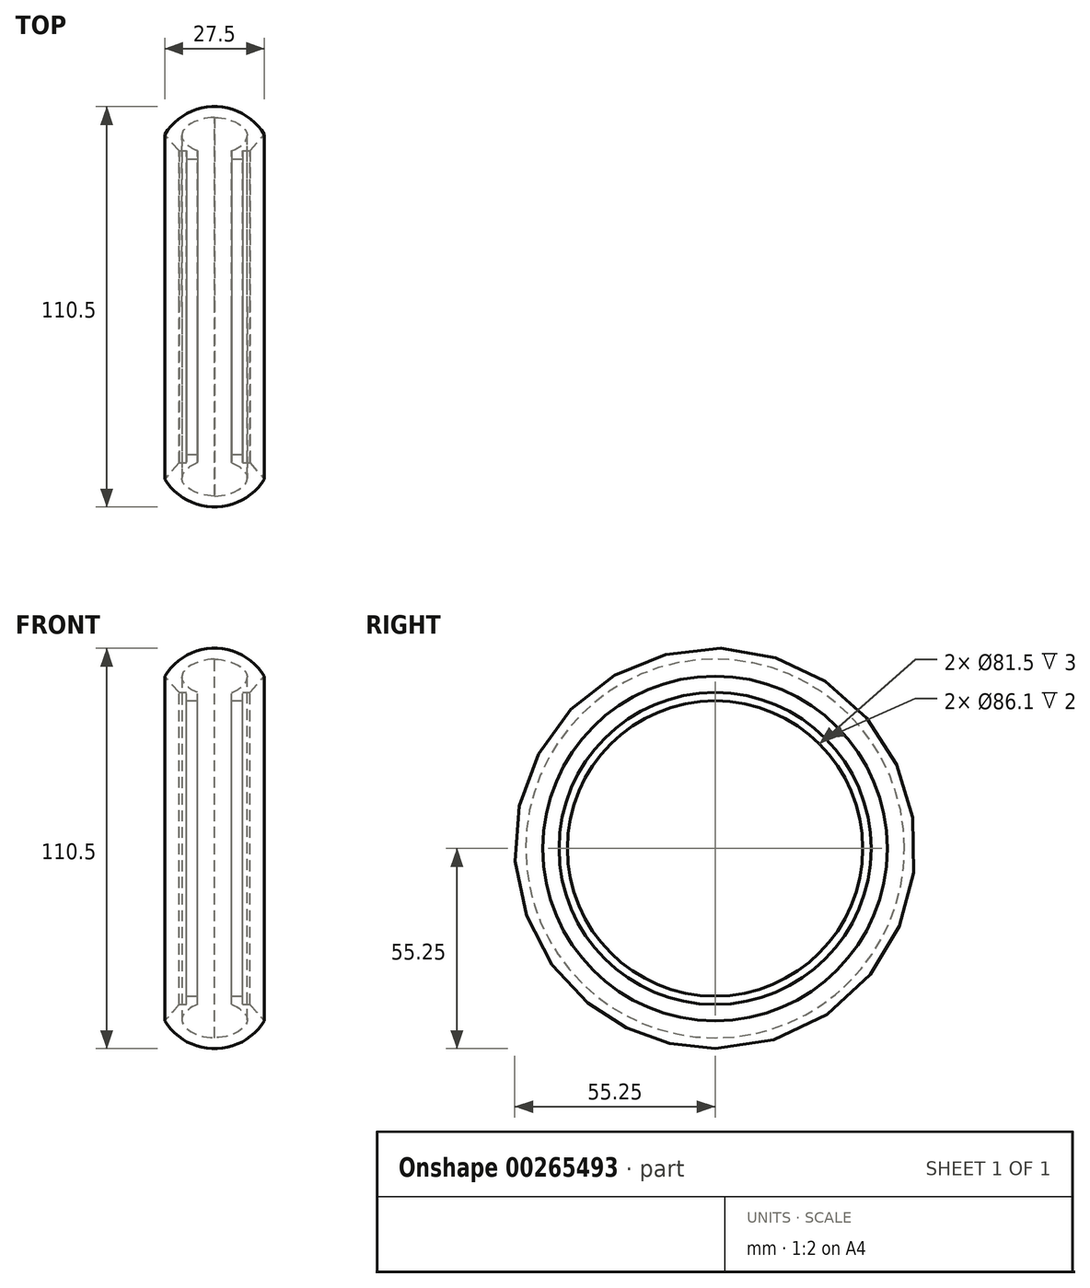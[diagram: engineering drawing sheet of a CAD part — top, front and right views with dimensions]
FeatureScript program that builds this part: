
annotation { "Feature Type Name" : "Feature", "Feature Type Description" : "" }
export const myFeature = defineFeature(function(context is Context, id is Id, definition is map)
    precondition{}
    {
        {
            var Q0;
            Q0=qCreatedBy(makeId("Front.planeOp"),FACE);
            var sketch = newSketch(context, id + "F0", { "sketchPlane" : qUnion([Q0])});
            skLineSegment(sketch, "E0", {"start": v(0, 0) * mm, "end": v(0, 55.25) * mm, "construction": true});
            skLineSegment(sketch, "E1", {"start": v(0, 55.25) * mm, "end": v(0, 40.75) * mm, "construction": true});
            skLineSegment(sketch, "E2", {"start": v(0, 40.75) * mm, "end": v(-7.75, 40.75) * mm, "construction": true});
            skLineSegment(sketch, "E3", {"start": v(-7.75, 40.75) * mm, "end": v(-7.75, 43.05) * mm});
            skLineSegment(sketch, "E4", {"start": v(-7.75, 43.05) * mm, "end": v(-9.75, 43.05) * mm});
            skLineSegment(sketch, "E5", {"start": v(-9.75, 43.05) * mm, "end": v(-9.75, 47.55) * mm, "construction": true});
            skLineSegment(sketch, "E6", {"start": v(-9.75, 47.55) * mm, "end": v(-13.75, 47.55) * mm, "construction": true});
            skLineSegment(sketch, "E7", {"start": v(-13.75, 47.55) * mm, "end": v(-9.75, 43.05) * mm});
            skLineSegment(sketch, "E8", {"start": v(-7.75, 40.75) * mm, "end": v(-4.75, 40.75) * mm});
            skLineSegment(sketch, "E9", {"start": v(-4.75, 40.75) * mm, "end": v(-4.75, 43.05) * mm});
            skArc(sketch, "E10", {"start": v(0, 55.25) * mm, "mid": v(-7.88, 53.2) * mm, "end": v(-13.75, 47.55) * mm});
            skLineSegment(sketch, "E11", {"start": v(0, 55.25) * mm, "end": v(0, 52.25) * mm, "construction": true});
            skLineSegment(sketch, "E12", {"start": v(-13.75, 47.55) * mm, "end": v(-10.75, 47.55) * mm, "construction": true});
            skLineSegment(sketch, "E13", {"start": v(-13.75, 47.55) * mm, "end": v(-9, 47.55) * mm, "construction": true});
            skFitSpline(sketch, "E14", {"points": [v(-4.75, 43.05) * mm, v(-9, 47.55) * mm, v(0, 52.25) * mm], "startDerivative": vector(-16.13, 6.14) * mm, "endDerivative": vector(25.97, 0.65) * mm});
            skArc(sketch, "E15.MirrorCS", {"start": v(0, 55.25) * mm, "mid": v(7.88, 53.2) * mm, "end": v(13.75, 47.55) * mm});
            skFitSpline(sketch, "E16.MirrorCS", {"points": [v(4.75, 43.05) * mm, v(9, 47.55) * mm, v(0, 52.25) * mm], "startDerivative": vector(16.13, 6.14) * mm, "endDerivative": vector(-25.97, 0.65) * mm});
            skLineSegment(sketch, "E17.MirrorCS", {"start": v(13.75, 47.55) * mm, "end": v(9.75, 43.05) * mm});
            skLineSegment(sketch, "E18.MirrorCS", {"start": v(7.75, 43.05) * mm, "end": v(9.75, 43.05) * mm});
            skLineSegment(sketch, "E19.MirrorCS", {"start": v(7.75, 40.75) * mm, "end": v(7.75, 43.05) * mm});
            skLineSegment(sketch, "E20.MirrorCS", {"start": v(7.75, 40.75) * mm, "end": v(4.75, 40.75) * mm});
            skLineSegment(sketch, "E21.MirrorCS", {"start": v(4.75, 40.75) * mm, "end": v(4.75, 43.05) * mm});
            skLineSegment(sketch, "E22", {"start": v(0, 0) * mm, "end": v(29.9, 0) * mm, "construction": true});
            skLineSegment(sketch, "E23", {"start": v(29.9, 0) * mm, "end": v(-38.2, 0) * mm, "construction": true});
            skSolve(sketch);
        }
        {
            var Q0;
            Q0=makeQuery(id+"F0.imprint","IMPRINT",FACE,{"disambiguationData":[TD([[makeQuery(id+"F0.imprint","IMPRINT",EDGE,{"derivedFrom":sQuery(id+"F0.wireOp",EDGE,"E3")}),-1.0]])]});
            var Q1;
            Q1=sQuery(id+"F0.wireOp",EDGE,"E23");
            revolve(context, id + "F1", {"entities" : qUnion([Q0]), "axis" : qUnion([Q1]), "revolveType" : RevolveType.FULL});
        }
    });
